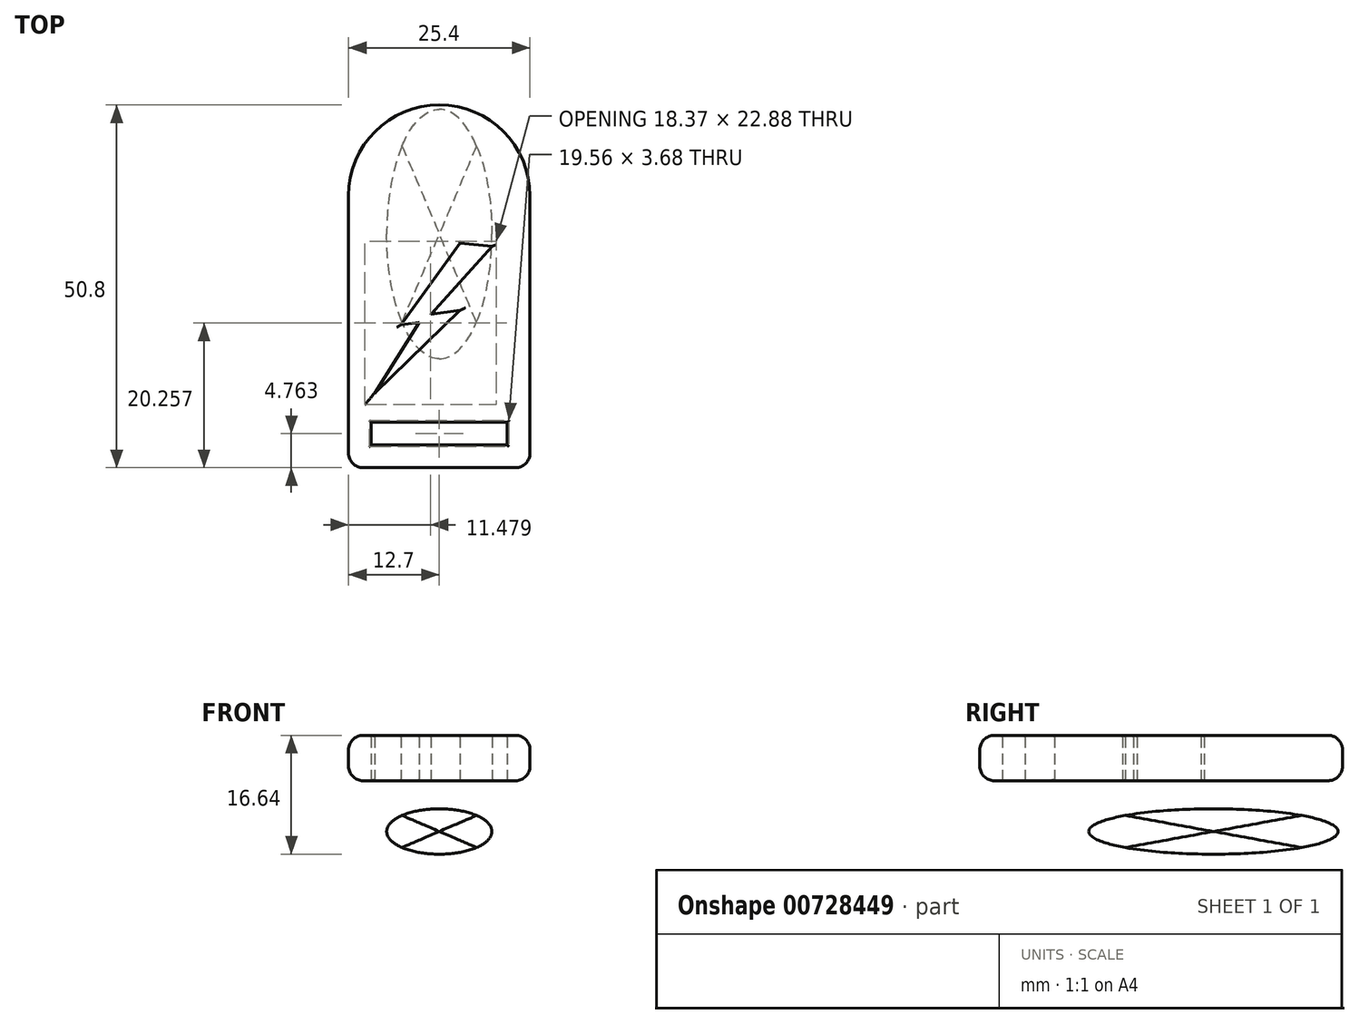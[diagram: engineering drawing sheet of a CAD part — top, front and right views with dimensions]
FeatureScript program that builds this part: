
annotation { "Feature Type Name" : "Feature", "Feature Type Description" : "" }
export const myFeature = defineFeature(function(context is Context, id is Id, definition is map)
    precondition{}
    {
        {
            var Q0;
            Q0=qCreatedBy(makeId("Top.planeOp"),FACE);
            var sketch = newSketch(context, id + "F0", { "sketchPlane" : qUnion([Q0])});
            skArc(sketch, "E0", {"start": v(12.7, 0) * mm, "mid": v(0, 12.7) * mm, "end": v(-12.7, 0) * mm});
            skLineSegment(sketch, "E1.top", {"start": v(-12.7, -38.1) * mm, "end": v(12.7, -38.1) * mm});
            skLineSegment(sketch, "E1.left", {"start": v(-12.7, 0) * mm, "end": v(-12.7, -38.1) * mm});
            skLineSegment(sketch, "E1.right", {"start": v(12.7, 0) * mm, "end": v(12.7, -38.1) * mm});
            skLineSegment(sketch, "E2", {"start": v(-12.7, -34.93) * mm, "end": v(-9.52, -34.93) * mm, "construction": true});
            skLineSegment(sketch, "E3", {"start": v(-9.53, -34.93) * mm, "end": v(-9.53, -38.1) * mm, "construction": true});
            skLineSegment(sketch, "E4.bottom", {"start": v(-9.52, -34.93) * mm, "end": v(9.53, -34.93) * mm});
            skLineSegment(sketch, "E4.top", {"start": v(-9.52, -31.75) * mm, "end": v(9.53, -31.75) * mm});
            skLineSegment(sketch, "E4.left", {"start": v(-9.52, -34.93) * mm, "end": v(-9.52, -31.75) * mm});
            skLineSegment(sketch, "E4.right", {"start": v(9.53, -34.93) * mm, "end": v(9.53, -31.75) * mm});
            skCircle(sketch, "E5", {"center": v(0, 0) * mm, "radius": 4.76 * mm});
            skLineSegment(sketch, "E6", {"start": v(-9.07, -27.64) * mm, "end": v(2.92, -16.06) * mm});
            skLineSegment(sketch, "E7", {"start": v(2.92, -16.06) * mm, "end": v(-1.2, -16.61) * mm});
            skLineSegment(sketch, "E8", {"start": v(-1.2, -16.61) * mm, "end": v(7.44, -7.09) * mm});
            skLineSegment(sketch, "E9", {"start": v(7.44, -7.09) * mm, "end": v(2.92, -6.67) * mm});
            skLineSegment(sketch, "E10", {"start": v(2.92, -6.67) * mm, "end": v(-5.35, -18.09) * mm});
            skLineSegment(sketch, "E11", {"start": v(-5.35, -18.09) * mm, "end": v(-2.83, -17.75) * mm});
            skLineSegment(sketch, "E12", {"start": v(-2.83, -17.75) * mm, "end": v(-9.07, -27.64) * mm});
            skSolve(sketch);
        }
        {
            var Q0;
            Q0=makeQuery(id+"F0.imprint","IMPRINT",FACE,{"disambiguationData":[TD([[makeQuery(id+"F0.imprint","IMPRINT",EDGE,{"derivedFrom":sQuery(id+"F0.wireOp",EDGE,"E0")}),1.0]])]});
            var Q1;
            Q1=makeQuery(id+"F0.imprint","IMPRINT",FACE,{"disambiguationData":[TD([[makeQuery(id+"F0.imprint","IMPRINT",EDGE,{"derivedFrom":sQuery(id+"F0.wireOp",EDGE,"E5")}),1.0]])]});
            extrude(context, id + "F1", {"entities" : qUnion([Q0, Q1]), "depth" : 6.35 * mm});
        }
        {
            var Q0;
            Q0=makeQuery(id+"F1.opExtrude","CAP_EDGE",EDGE,{"disambiguationData":[OSD([sQuery(id+"F0.wireOp",EDGE,"E1.left")])],"isStart":false});
            var Q1;
            Q1=makeQuery(id+"F1.opExtrude","CAP_EDGE",EDGE,{"disambiguationData":[OSD([sQuery(id+"F0.wireOp",EDGE,"E1.top")])],"isStart":false});
            var Q2;
            Q2=makeQuery(id+"F1.opExtrude","CAP_EDGE",EDGE,{"disambiguationData":[OSD([sQuery(id+"F0.wireOp",EDGE,"E1.top")])],"isStart":true});
            var Q3;
            Q3=makeQuery(id+"F1.opExtrude","SWEPT_EDGE",EDGE,{"disambiguationData":[OSD([sQuery(id+"F0.wireOp",EDGE,"E1.top"),sQuery(id+"F0.wireOp",EDGE,"E1.right")])]});
            var Q4;
            Q4=makeQuery(id+"F1.opExtrude","SWEPT_EDGE",EDGE,{"disambiguationData":[OSD([sQuery(id+"F0.wireOp",EDGE,"E1.top"),sQuery(id+"F0.wireOp",EDGE,"E1.left")])]});
            var Q5;
            Q5=makeQuery(id+"F1.opExtrude","CAP_EDGE",EDGE,{"disambiguationData":[OSD([sQuery(id+"F0.wireOp",EDGE,"E1.left")])],"isStart":true});
            fillet(context, id + "F2", {"entities" : qUnion([Q0, Q1, Q2, Q3, Q4, Q5]), "radius" : 2.03 * mm, "tangentPropagation" : true, "allowEdgeOverflow" : false});
        }
        {
            var Q0;
            Q0=makeQuery(id+"F1.opExtrude","CAP_EDGE",EDGE,{"disambiguationData":[OSD([sQuery(id+"F0.wireOp",EDGE,"E4.top")])],"isStart":false});
            var Q1;
            Q1=makeQuery(id+"F1.opExtrude","CAP_EDGE",EDGE,{"disambiguationData":[OSD([sQuery(id+"F0.wireOp",EDGE,"E4.bottom")])],"isStart":false});
            var Q2;
            Q2=makeQuery(id+"F1.opExtrude","CAP_EDGE",EDGE,{"disambiguationData":[OSD([sQuery(id+"F0.wireOp",EDGE,"E4.left")])],"isStart":false});
            var Q3;
            Q3=makeQuery(id+"F1.opExtrude","CAP_EDGE",EDGE,{"disambiguationData":[OSD([sQuery(id+"F0.wireOp",EDGE,"E4.right")])],"isStart":false});
            var Q4;
            Q4=makeQuery(id+"F1.opExtrude","CAP_EDGE",EDGE,{"disambiguationData":[OSD([sQuery(id+"F0.wireOp",EDGE,"E4.left")])],"isStart":true});
            var Q5;
            Q5=makeQuery(id+"F1.opExtrude","CAP_EDGE",EDGE,{"disambiguationData":[OSD([sQuery(id+"F0.wireOp",EDGE,"E4.top")])],"isStart":true});
            var Q6;
            Q6=makeQuery(id+"F1.opExtrude","CAP_EDGE",EDGE,{"disambiguationData":[OSD([sQuery(id+"F0.wireOp",EDGE,"E4.bottom")])],"isStart":true});
            var Q7;
            Q7=makeQuery(id+"F1.opExtrude","CAP_EDGE",EDGE,{"disambiguationData":[OSD([sQuery(id+"F0.wireOp",EDGE,"E4.right")])],"isStart":true});
            var Q8;
            Q8=makeQuery(id+"F1.opExtrude","CAP_EDGE",EDGE,{"disambiguationData":[OSD([sQuery(id+"F0.wireOp",EDGE,"E12")])],"isStart":true});
            var Q9;
            Q9=makeQuery(id+"F1.opExtrude","CAP_EDGE",EDGE,{"disambiguationData":[OSD([sQuery(id+"F0.wireOp",EDGE,"E10")])],"isStart":true});
            var Q10;
            Q10=makeQuery(id+"F1.opExtrude","CAP_EDGE",EDGE,{"disambiguationData":[OSD([sQuery(id+"F0.wireOp",EDGE,"E11")])],"isStart":true});
            var Q11;
            Q11=makeQuery(id+"F1.opExtrude","CAP_EDGE",EDGE,{"disambiguationData":[OSD([sQuery(id+"F0.wireOp",EDGE,"E8")])],"isStart":true});
            var Q12;
            Q12=makeQuery(id+"F1.opExtrude","CAP_EDGE",EDGE,{"disambiguationData":[OSD([sQuery(id+"F0.wireOp",EDGE,"E7")])],"isStart":true});
            var Q13;
            Q13=makeQuery(id+"F1.opExtrude","CAP_EDGE",EDGE,{"disambiguationData":[OSD([sQuery(id+"F0.wireOp",EDGE,"E6")])],"isStart":true});
            var Q14;
            Q14=makeQuery(id+"F1.opExtrude","CAP_EDGE",EDGE,{"disambiguationData":[OSD([sQuery(id+"F0.wireOp",EDGE,"E9")])],"isStart":true});
            var Q15;
            Q15=makeQuery(id+"F1.opExtrude","CAP_EDGE",EDGE,{"disambiguationData":[OSD([sQuery(id+"F0.wireOp",EDGE,"E9")])],"isStart":false});
            var Q16;
            Q16=makeQuery(id+"F1.opExtrude","CAP_EDGE",EDGE,{"disambiguationData":[OSD([sQuery(id+"F0.wireOp",EDGE,"E8")])],"isStart":false});
            var Q17;
            Q17=makeQuery(id+"F1.opExtrude","CAP_EDGE",EDGE,{"disambiguationData":[OSD([sQuery(id+"F0.wireOp",EDGE,"E10")])],"isStart":false});
            var Q18;
            Q18=makeQuery(id+"F1.opExtrude","CAP_EDGE",EDGE,{"disambiguationData":[OSD([sQuery(id+"F0.wireOp",EDGE,"E6")])],"isStart":false});
            var Q19;
            Q19=makeQuery(id+"F1.opExtrude","CAP_EDGE",EDGE,{"disambiguationData":[OSD([sQuery(id+"F0.wireOp",EDGE,"E12")])],"isStart":false});
            var Q20;
            Q20=makeQuery(id+"F1.opExtrude","CAP_EDGE",EDGE,{"disambiguationData":[OSD([sQuery(id+"F0.wireOp",EDGE,"E7")])],"isStart":false});
            var Q21;
            Q21=makeQuery(id+"F1.opExtrude","CAP_EDGE",EDGE,{"disambiguationData":[OSD([sQuery(id+"F0.wireOp",EDGE,"E11")])],"isStart":false});
            fillet(context, id + "F3", {"entities" : qUnion([Q0, Q1, Q2, Q3, Q4, Q5, Q6, Q7, Q8, Q9, Q10, Q11, Q12, Q13, Q14, Q15, Q16, Q17, Q18, Q19, Q20, Q21]), "radius" : 0.25 * mm, "tangentPropagation" : true, "allowEdgeOverflow" : false});
        }
        {
            var Q0;
            Q0=qCreatedBy(makeId("Top.planeOp"),FACE);
            cPlane(context, id + "F4", {"entities" : qUnion([Q0]), "cplaneType" : CPlaneType.OFFSET, "offset" : 7.11 * mm, "oppositeDirection" : true, "width" : 152.4 * mm, "height" : 152.4 * mm});
        }
        {
            var Q0;
            Q0=qCreatedBy(makeId("Front.planeOp"),FACE);
            cPlane(context, id + "F5", {"entities" : qUnion([Q0]), "cplaneType" : CPlaneType.OFFSET, "offset" : 5.38 * mm, "width" : 152.4 * mm, "height" : 152.4 * mm});
        }
        {
            var Q0;
            Q0=qCreatedBy(id+"F4.planeOp",FACE);
            var sketch = newSketch(context, id + "F6", { "sketchPlane" : qUnion([Q0])});
            skPoint(sketch, "E13", {"position": v(0, -5.38) * mm});
            skSolve(sketch);
        }
        {
            var Q0;
            Q0=qCreatedBy(id+"F4.planeOp",FACE);
            var sketch = newSketch(context, id + "F7", { "sketchPlane" : qUnion([Q0])});
            skEllipse(sketch, "E14", {"center": v(0, -5.38) * mm, "majorRadius": 17.46 * mm, "minorRadius": 7.37 * mm, "majorAxis": v(0, 1)});
            skSolve(sketch);
        }
        {
            var Q0;
            Q0=qCreatedBy(id+"F5.planeOp",FACE);
            var sketch = newSketch(context, id + "F8", { "sketchPlane" : qUnion([Q0])});
            skEllipse(sketch, "E15", {"center": v(0, -7.11) * mm, "majorRadius": 7.37 * mm, "minorRadius": 3.18 * mm, "majorAxis": v(1, 0)});
            skSolve(sketch);
        }
        {
            var Q0;
            Q0=qCreatedBy(makeId("Right.planeOp"),FACE);
            var sketch = newSketch(context, id + "F9", { "sketchPlane" : qUnion([Q0])});
            skEllipse(sketch, "E16", {"center": v(-5.38, -7.11) * mm, "majorRadius": 17.46 * mm, "minorRadius": 3.18 * mm, "majorAxis": v(-1, 0)});
            skSolve(sketch);
        }
        {
            var Q0;
            Q0=qSketchRegion(id+"F7",true);
            var Q1;
            Q1=sQuery(id+"F7.wireOp",EDGE,"E14");
            extrude(context, id + "F10", {"entities" : qUnion([Q0]), "surfaceEntities" : qUnion([Q1]), "endBound" : BoundingType.SYMMETRIC, "depth" : 6.35 * mm});
        }
        {
            var Q0;
            Q0=qSketchRegion(id+"F8",true);
            extrude(context, id + "F11", {"entities" : qUnion([Q0]), "endBound" : BoundingType.SYMMETRIC, "depth" : 34.92 * mm});
        }
        {
            var Q0;
            Q0=qSketchRegion(id+"F9",true);
            extrude(context, id + "F12", {"entities" : qUnion([Q0]), "endBound" : BoundingType.SYMMETRIC, "depth" : 14.73 * mm});
        }
        {
            var Q0;
            Q0=makeQuery(id+"F11.opExtrude","SWEPT_BODY",BODY,{"disambiguationData":[OSD([sQuery(id+"F8.wireOp",EDGE,"E15")])]});
            var Q1;
            Q1=makeQuery(id+"F12.opExtrude","SWEPT_BODY",BODY,{"disambiguationData":[OSD([sQuery(id+"F9.wireOp",EDGE,"E16")])]});
            var Q2;
            Q2=makeQuery(id+"F10.opExtrude","SWEPT_BODY",BODY,{"disambiguationData":[OSD([sQuery(id+"F7.wireOp",EDGE,"E14")])]});
            booleanBodies(context, id + "F13", {"operationType" : BooleanOperationType.INTERSECTION, "tools" : qUnion([Q0, Q1, Q2])});
        }
    });
